# Revit family: Überspannungsableiter 3-polig + NPE
name_source: partatom
category: Generic Models
revit_build: Autodesk Revit 2015 (Build: 20140606_1530(x64)
units: mm (PartAtom-declared; Revit-internal decimal feet)

## types (2) — shared parameters
Cut depth = 12 mm  [stored 0.0393701 ft]
Diameter = 7 mm  [stored 0.0229659 ft]
Height = 60 mm  [stored 0.19685 ft]
Length = 71 mm
Manufacturer = OBO Bettermann
Material = OBO PA 6 GF20
Material 2 = OBO PA GF20 RAL 5017
URL = http://www.obo-bettermann.com
Width = 90 mm  [stored 0.295276 ft]

## per-type parameters (varying)
| type | GTIN | Manufacturer Art.No. |
| V10-C 3+NPE | 4012195363903 | 5094920 |
| V10-C 3+NPE-320 | 4012195363934 | 5094924 |

note: column(s) folded — value = type name in every type: Article Type

note: [stored X ft] marks values corroborated as IEEE doubles in the binary element streams (Revit-internal decimal feet)

## geometry (parser evidence)
native form markers: Sweep x2
no freeform markers — native parametric forms only
